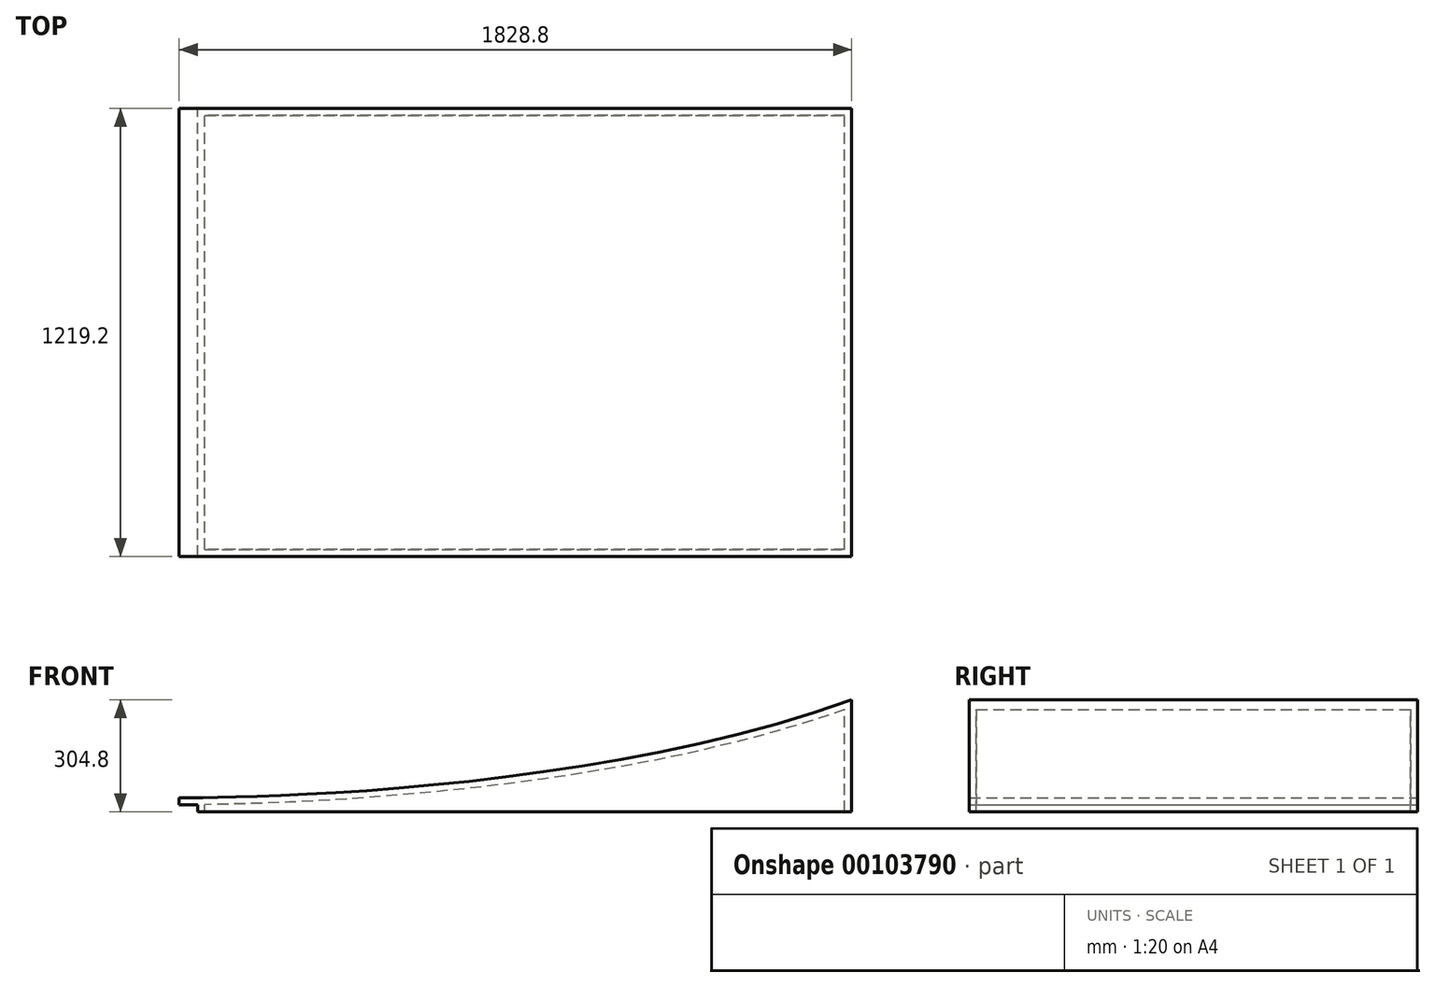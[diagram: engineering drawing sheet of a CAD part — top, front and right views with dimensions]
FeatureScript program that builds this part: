
annotation { "Feature Type Name" : "Feature", "Feature Type Description" : "" }
export const myFeature = defineFeature(function(context is Context, id is Id, definition is map)
    precondition{}
    {
        {
            var Q0;
            Q0=qCreatedBy(makeId("Front.planeOp"),FACE);
            var sketch = newSketch(context, id + "F0", { "sketchPlane" : qUnion([Q0])});
            skLineSegment(sketch, "E0", {"start": v(0, 0) * mm, "end": v(0, 304.8) * mm});
            skLineSegment(sketch, "E1", {"start": v(-1828.8, 0) * mm, "end": v(-1778, 0) * mm, "construction": true});
            skLineSegment(sketch, "E2", {"start": v(-1778, 0) * mm, "end": v(-1778, 19.05) * mm});
            skLineSegment(sketch, "E3", {"start": v(-1778, 19.05) * mm, "end": v(0, 19.05) * mm, "construction": true});
            skLineSegment(sketch, "E4", {"start": v(-1778, 19.05) * mm, "end": v(-1828.8, 19.05) * mm});
            skLineSegment(sketch, "E5", {"start": v(-1778, 0) * mm, "end": v(0, 0) * mm});
            skFitSpline(sketch, "E6", {"points": [v(0, 304.8) * mm, v(-1828.8, 38.1) * mm], "startDerivative": vector(-2287.3, -824.38) * mm, "endDerivative": vector(-125.4, -2.79) * mm});
            skLineSegment(sketch, "E7", {"start": v(-1828.8, 38.1) * mm, "end": v(-1828.8, 19.05) * mm});
            skPoint(sketch, "E8", {"position": v(-1803.4, 19.05) * mm});
            skSolve(sketch);
        }
        {
            var Q0;
            Q0=makeQuery(id+"F0.imprint","IMPRINT",FACE,{"disambiguationData":[TD([[makeQuery(id+"F0.imprint","IMPRINT",EDGE,{"derivedFrom":sQuery(id+"F0.wireOp",EDGE,"E0")}),1.0]])]});
            extrude(context, id + "F1", {"entities" : qUnion([Q0]), "depth" : 1219.2 * mm});
        }
        {
            var Q0;
            Q0=makeQuery(id+"F1.opExtrude","SWEPT_FACE",FACE,{"disambiguationData":[OSD([sQuery(id+"F0.wireOp",EDGE,"E5")])]});
            shell(context, id + "F2", {"entities" : qUnion([Q0]), "thickness" : 19.05 * mm});
        }
    });
